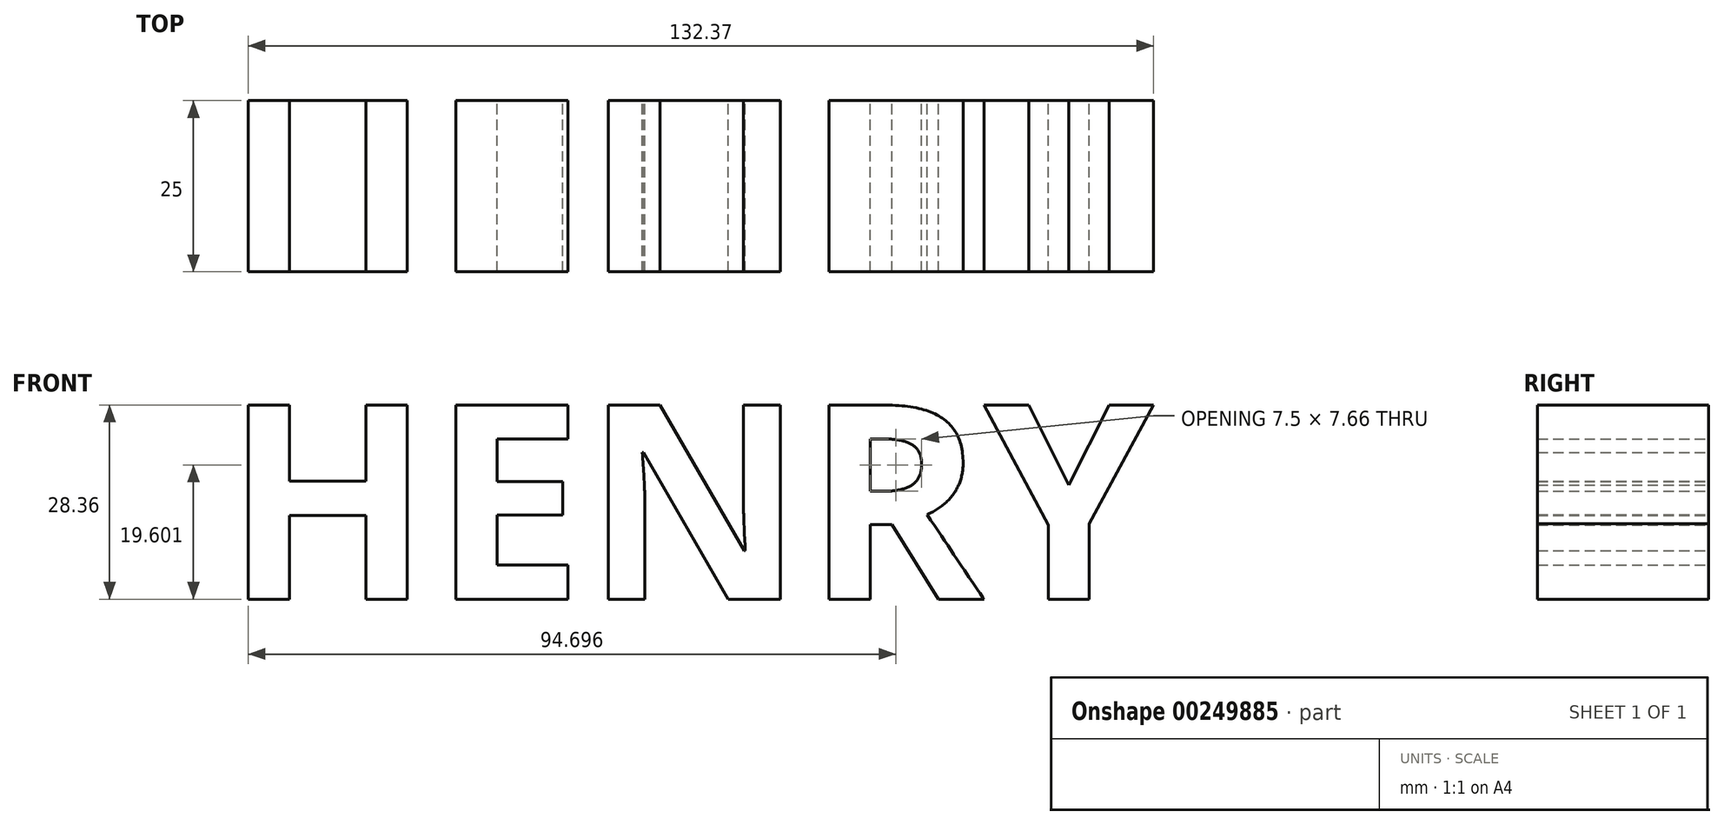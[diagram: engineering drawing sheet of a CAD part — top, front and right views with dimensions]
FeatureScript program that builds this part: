
annotation { "Feature Type Name" : "Feature", "Feature Type Description" : "" }
export const myFeature = defineFeature(function(context is Context, id is Id, definition is map)
    precondition{}
    {
        {
            var Q0;
            Q0=qCreatedBy(makeId("Front.planeOp"),FACE);
            var sketch = newSketch(context, id + "F0", { "sketchPlane" : qUnion([Q0])});
            skText(sketch, "E0", { "text": "HENRY", "fontName": "OpenSans-Bold.ttf"});
            const initialGuessF0  = {"E0": [-0.06176, 0, 1, 0, 0.0286]};
            skSetInitialGuess(sketch, initialGuessF0);
            skSolve(sketch);
        }
        {
            var Q0;
            Q0=makeQuery(id+"F0.imprint","IMPRINT",FACE,{"disambiguationData":[TD([[makeQuery(id+"F0.imprint","IMPRINT",EDGE,{"derivedFrom":sQuery(id+"F0.wireOp",EDGE,"E0.sketch_text.stroke-0")}),-1.0]])]});
            var Q1;
            Q1=makeQuery(id+"F0.imprint","IMPRINT",FACE,{"disambiguationData":[TD([[makeQuery(id+"F0.imprint","IMPRINT",EDGE,{"derivedFrom":sQuery(id+"F0.wireOp",EDGE,"E0.sketch_text.stroke-12")}),-1.0]])]});
            var Q2;
            Q2=makeQuery(id+"F0.imprint","IMPRINT",FACE,{"disambiguationData":[TD([[makeQuery(id+"F0.imprint","IMPRINT",EDGE,{"derivedFrom":sQuery(id+"F0.wireOp",EDGE,"E0.sketch_text.stroke-24")}),-1.0]])]});
            var Q3;
            Q3=makeQuery(id+"F0.imprint","IMPRINT",FACE,{"disambiguationData":[TD([[makeQuery(id+"F0.imprint","IMPRINT",EDGE,{"derivedFrom":sQuery(id+"F0.wireOp",EDGE,"E0.sketch_text.stroke-38")}),-1.0]])]});
            var Q4;
            Q4=makeQuery(id+"F0.imprint","IMPRINT",FACE,{"disambiguationData":[TD([[makeQuery(id+"F0.imprint","IMPRINT",EDGE,{"derivedFrom":sQuery(id+"F0.wireOp",EDGE,"E0.sketch_text.stroke-57")}),-1.0]])]});
            extrude(context, id + "F1", {"entities" : qUnion([Q0, Q1, Q2, Q3, Q4]), "depth" : 25 * mm});
        }
    });
